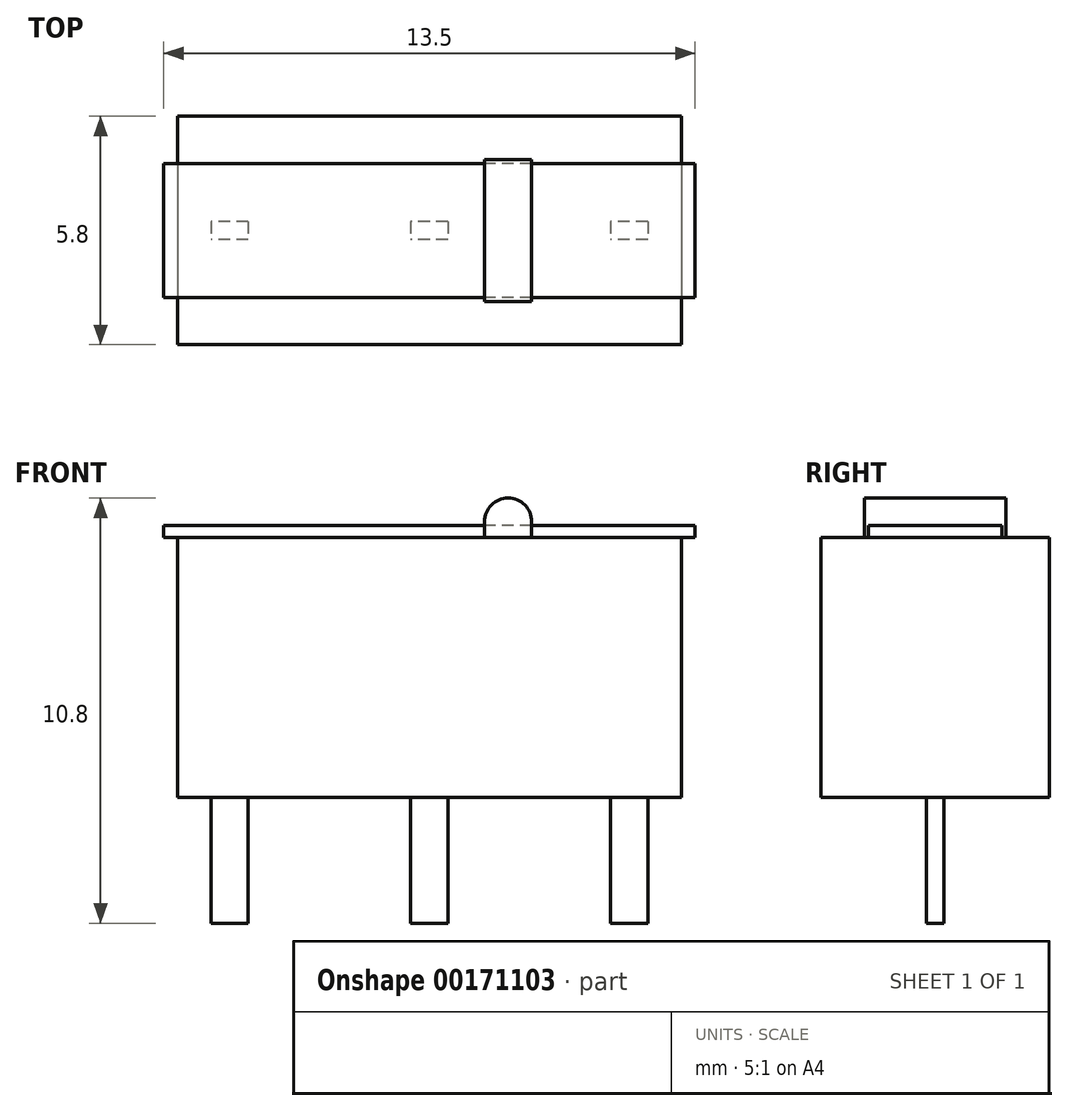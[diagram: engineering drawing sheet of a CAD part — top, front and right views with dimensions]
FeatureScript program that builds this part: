
annotation { "Feature Type Name" : "Feature", "Feature Type Description" : "" }
export const myFeature = defineFeature(function(context is Context, id is Id, definition is map)
    precondition{}
    {
        {
            var Q0;
            Q0=qCreatedBy(makeId("Top.planeOp"),FACE);
            var sketch = newSketch(context, id + "F0", { "sketchPlane" : qUnion([Q0])});
            skLineSegment(sketch, "E0.bottom", {"start": v(6.4, 2.9) * mm, "end": v(-6.4, 2.9) * mm});
            skLineSegment(sketch, "E0.top", {"start": v(6.4, -2.9) * mm, "end": v(-6.4, -2.9) * mm});
            skLineSegment(sketch, "E0.left", {"start": v(6.4, 2.9) * mm, "end": v(6.4, -2.9) * mm});
            skLineSegment(sketch, "E0.right", {"start": v(-6.4, 2.9) * mm, "end": v(-6.4, -2.9) * mm});
            skPoint(sketch, "E0.middle", {"position": v(0, 0) * mm});
            skSolve(sketch);
        }
        {
            var Q0;
            Q0 = qSketchRegion(id + "F0", true);
            extrude(context, id + "F1", {"entities" : qUnion([Q0]), "depth" : 6.6 * mm});
        }
        {
            var Q0;
            Q0=makeQuery(id+"F1.opExtrude","CAP_FACE",FACE,{"disambiguationData":[OSD([sQuery(id+"F0.wireOp",EDGE,"E0.bottom"),sQuery(id+"F0.wireOp",EDGE,"E0.top"),sQuery(id+"F0.wireOp",EDGE,"E0.left"),sQuery(id+"F0.wireOp",EDGE,"E0.right")])],"isStart":true});
            var sketch = newSketch(context, id + "F2", { "sketchPlane" : qUnion([Q0])});
            skLineSegment(sketch, "E1.bottom", {"start": v(-4.6, -0.23) * mm, "end": v(-5.55, -0.23) * mm});
            skLineSegment(sketch, "E1.top", {"start": v(-4.6, 0.22) * mm, "end": v(-5.55, 0.22) * mm});
            skLineSegment(sketch, "E1.left", {"start": v(-4.6, -0.23) * mm, "end": v(-4.6, 0.22) * mm});
            skLineSegment(sketch, "E1.right", {"start": v(-5.55, -0.23) * mm, "end": v(-5.55, 0.22) * mm});
            skPoint(sketch, "E1.middle", {"position": v(-5.08, 0) * mm});
            skLineSegment(sketch, "E2.bottom", {"start": v(0.48, -0.22) * mm, "end": v(-0.47, -0.22) * mm});
            skLineSegment(sketch, "E2.top", {"start": v(0.47, 0.23) * mm, "end": v(-0.48, 0.23) * mm});
            skLineSegment(sketch, "E2.left", {"start": v(0.47, -0.22) * mm, "end": v(0.47, 0.23) * mm});
            skLineSegment(sketch, "E2.right", {"start": v(-0.47, -0.22) * mm, "end": v(-0.48, 0.23) * mm});
            skPoint(sketch, "E2.middle", {"position": v(0, 0) * mm});
            skLineSegment(sketch, "E3.bottom", {"start": v(5.55, -0.22) * mm, "end": v(4.6, -0.22) * mm});
            skLineSegment(sketch, "E3.top", {"start": v(5.55, 0.23) * mm, "end": v(4.6, 0.23) * mm});
            skLineSegment(sketch, "E3.left", {"start": v(5.55, -0.23) * mm, "end": v(5.55, 0.22) * mm});
            skLineSegment(sketch, "E3.right", {"start": v(4.6, -0.23) * mm, "end": v(4.6, 0.22) * mm});
            skPoint(sketch, "E3.middle", {"position": v(5.07, 0) * mm});
            skLineSegment(sketch, "E4", {"start": v(-4.6, -0.23) * mm, "end": v(-0.47, -0.23) * mm});
            skLineSegment(sketch, "E5", {"start": v(0.48, -0.23) * mm, "end": v(4.6, -0.23) * mm});
            skSolve(sketch);
        }
        {
            var Q0;
            Q0=makeQuery(id+"F2.imprint","IMPRINT",FACE,{"disambiguationData":[TD([[makeQuery(id+"F2.imprint","IMPRINT",EDGE,{"derivedFrom":sQuery(id+"F2.wireOp",EDGE,"E1.bottom")}),-1.0]])]});
            var Q1;
            Q1=makeQuery(id+"F2.imprint","IMPRINT",FACE,{"disambiguationData":[TD([[makeQuery(id+"F2.imprint","IMPRINT",EDGE,{"derivedFrom":sQuery(id+"F2.wireOp",EDGE,"E2.bottom")}),-1.0]])]});
            var Q2;
            Q2=makeQuery(id+"F2.imprint","IMPRINT",FACE,{"disambiguationData":[TD([[makeQuery(id+"F2.imprint","IMPRINT",EDGE,{"derivedFrom":sQuery(id+"F2.wireOp",EDGE,"E3.bottom")}),-1.0]])]});
            extrude(context, id + "F3", {"entities" : qUnion([Q0, Q1, Q2]), "operationType" : NewBodyOperationType.ADD, "depth" : 3.2 * mm});
        }
        {
            var Q0;
            Q0=makeQuery(id+"F1.opExtrude","CAP_FACE",FACE,{"disambiguationData":[OSD([sQuery(id+"F0.wireOp",EDGE,"E0.bottom"),sQuery(id+"F0.wireOp",EDGE,"E0.top"),sQuery(id+"F0.wireOp",EDGE,"E0.left"),sQuery(id+"F0.wireOp",EDGE,"E0.right")])],"isStart":false});
            var sketch = newSketch(context, id + "F4", { "sketchPlane" : qUnion([Q0])});
            skLineSegment(sketch, "E6.bottom", {"start": v(2.6, 1.8) * mm, "end": v(1.4, 1.8) * mm});
            skLineSegment(sketch, "E6.top", {"start": v(2.6, -1.8) * mm, "end": v(1.4, -1.8) * mm});
            skLineSegment(sketch, "E6.left", {"start": v(2.6, 1.8) * mm, "end": v(2.6, -1.8) * mm});
            skLineSegment(sketch, "E6.right", {"start": v(1.4, 1.8) * mm, "end": v(1.4, -1.8) * mm});
            skLineSegment(sketch, "E7", {"start": v(-6.4, 0) * mm, "end": v(6.4, 0) * mm, "construction": true});
            skSolve(sketch);
        }
        {
            var Q0;
            Q0=makeQuery(id+"F4.imprint","IMPRINT",FACE,{"disambiguationData":[TD([[makeQuery(id+"F4.imprint","IMPRINT",EDGE,{"derivedFrom":sQuery(id+"F4.wireOp",EDGE,"E6.bottom")}),1.0]])]});
            extrude(context, id + "F5", {"entities" : qUnion([Q0]), "operationType" : NewBodyOperationType.ADD, "depth" : 1 * mm});
        }
        {
            var Q0;
            Q0=makeQuery(id+"F5.opExtrude","CAP_EDGE",EDGE,{"disambiguationData":[OSD([sQuery(id+"F4.wireOp",EDGE,"E6.right")])],"isStart":false});
            var Q1;
            Q1=makeQuery(id+"F5.opExtrude","CAP_EDGE",EDGE,{"disambiguationData":[OSD([sQuery(id+"F4.wireOp",EDGE,"E6.left")])],"isStart":false});
            fillet(context, id + "F6", {"entities" : qUnion([Q0, Q1]), "radius" : 0.6 * mm, "tangentPropagation" : true, "allowEdgeOverflow" : false});
        }
        {
            var Q0;
            Q0=makeQuery(id+"F1.opExtrude","CAP_FACE",FACE,{"disambiguationData":[OSD([sQuery(id+"F0.wireOp",EDGE,"E0.bottom"),sQuery(id+"F0.wireOp",EDGE,"E0.top"),sQuery(id+"F0.wireOp",EDGE,"E0.left"),sQuery(id+"F0.wireOp",EDGE,"E0.right")])],"isStart":false});
            var sketch = newSketch(context, id + "F7", { "sketchPlane" : qUnion([Q0])});
            skLineSegment(sketch, "E8.bottom", {"start": v(6.75, -1.7) * mm, "end": v(-6.75, -1.7) * mm});
            skLineSegment(sketch, "E8.top", {"start": v(6.75, 1.7) * mm, "end": v(-6.75, 1.7) * mm});
            skLineSegment(sketch, "E8.left", {"start": v(6.75, -1.7) * mm, "end": v(6.75, 1.7) * mm});
            skLineSegment(sketch, "E8.right", {"start": v(-6.75, -1.7) * mm, "end": v(-6.75, 1.7) * mm});
            skPoint(sketch, "E8.middle", {"position": v(0, 0) * mm});
            skSolve(sketch);
        }
        {
            var Q0;
            Q0 = qSketchRegion(id + "F7", true);
            extrude(context, id + "F8", {"entities" : qUnion([Q0]), "depth" : 0.3 * mm});
        }
    });
